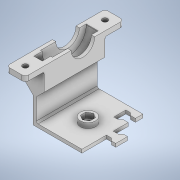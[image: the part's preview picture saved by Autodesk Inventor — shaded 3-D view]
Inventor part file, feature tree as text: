
AUTODESK INVENTOR PART (.ipt)
format: ipt  version: 2021 (Build 250183000, 183)  size: 324,096 bytes
history: native  units: mm
features: extrude x11, sketch x9, fillet x6, other x3, shell x1, chamfer x1, projected_geometry x1
ambient origin geometry x8: Origin, YZ Plane, XZ Plane, XY Plane, X Axis, Y Axis, Z Axis, Center Point
bodies: Body1 (feature_tree)
feature tree (32):
  other  "Твердое тело1"
  extrude  "Выдавливание1"  Depth=2.0mm
  extrude  "Выдавливание2"  Depth=20.0mm
  shell  "Оболочка1"  Thickness=2.0mm
  fillet  "Сопряжение1"  Radius=27.0mm
  extrude  "Выдавливание3"  Depth=26.1mm TaperAngle=0.0deg
  sketch  "Эскиз4"
  extrude  "Выдавливание4"  Depth=7.1mm
  extrude  "Выдавливание5"  Depth=22.1mm
  fillet  "Сопряжение2"  Radius=2.0mm
  fillet  "Сопряжение3"  Radius=2.0mm
  chamfer  "Фаска1"  Distance=13.5mm
  extrude  "Выдавливание7"  Depth=2.0mm
  extrude  "Выдавливание8"  Depth=11.0mm
  extrude  "Выдавливание9"  Depth=14.0mm
  other  "Непосредственное редактирование1"
  sketch  "Эскиз10"
  extrude  "Выдавливание10"  TaperAngle=0.0deg  [1 undecoded]
  extrude  "Выдавливание11"  Depth=3.0mm
  fillet  "Сопряжение6"  Radius=7.0mm
  extrude  "Выдавливание12"  Depth=2.5mm
  fillet  "Сопряжение7"  Radius=4.0mm
  fillet  "Сопряжение8"  Radius=7.0mm
  sketch  "Эскиз1"
  sketch  "Эскиз2"
  projected_geometry  "Спроецированная петля1"
  sketch  "Эскиз3"
  sketch  "Эскиз7"
  sketch  "Эскиз8"
  sketch  "Эскиз9"
  sketch  "Эскиз12"
  other  "Перенос1"
note: 1 required parameter value undecoded (feature->parameter linkage not recoverable at this tier; creation-order binding heuristic only, values carry confidence <= 0.55)
